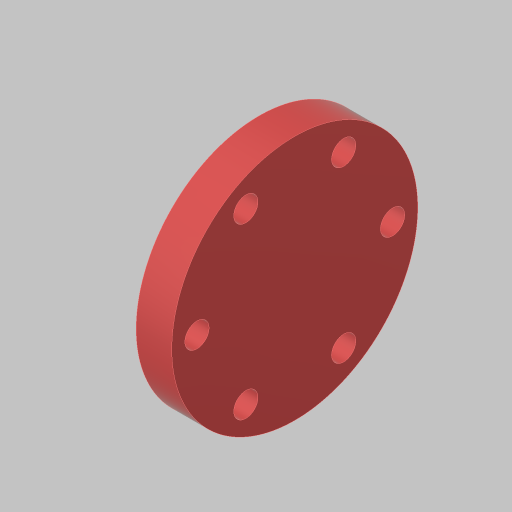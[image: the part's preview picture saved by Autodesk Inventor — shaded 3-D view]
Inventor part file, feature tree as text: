
AUTODESK INVENTOR PART (.ipt)
format: ipt  version: 2023.5 (Build 275446000, 446)  size: 253,440 bytes
history: native  units: in
note: dims shown in document units (in); Inventor stores cm internally (conversion verified against a paired STEP export)
features: sketch x4, hole x3, extrude x2, projected_geometry x1, other x1
ambient origin geometry x8: Origin, YZ Plane, XZ Plane, XY Plane, X Axis, Y Axis, Z Axis, Center Point
bodies: Solid1 (feature_tree)
feature tree (11):
  extrude  "Extrusion1"  Depth=1.0in TaperAngle=0.0deg
  sketch  "Sketch2"  dims[d3=0.1562in]
  hole  "Hole1"  [1 undecoded]
  hole  "Hole2"  [1 undecoded]
  extrude  "Extrusion2"  Depth=1.0in TaperAngle=360.0deg
  hole  "Hole4"  [1 undecoded]
  sketch  "Sketch1"  dims[d0=0.875in d1=1.0in d2=0.0in]
  sketch  "Sketch4"  dims[d4=0.156in d5=0.38in d6=0.385in d7=0.25in d8=0.563in d9=1.0in d10=0.8108in]
  projected_geometry  "Projected Loop1"
  sketch  "Sketch6"  dims[d11=0.145in d12=0.38in d13=0.375in d14=0.25in d15=0.5635in d16=1.0in d17=0.8108in d19=0.3189in d20=0.0in d37=1.75in d38=2.3622in d40=360.0deg d42=0.2165in d43=0.75in d44=0.375in d45=0.25in d46=0.5635in d47=1.0in d48=0.8108in]
  other  "Cut-Extrude8"
note: 3 required parameter values undecoded (feature->parameter linkage not recoverable at this tier; creation-order binding heuristic only, values carry confidence <= 0.55)
